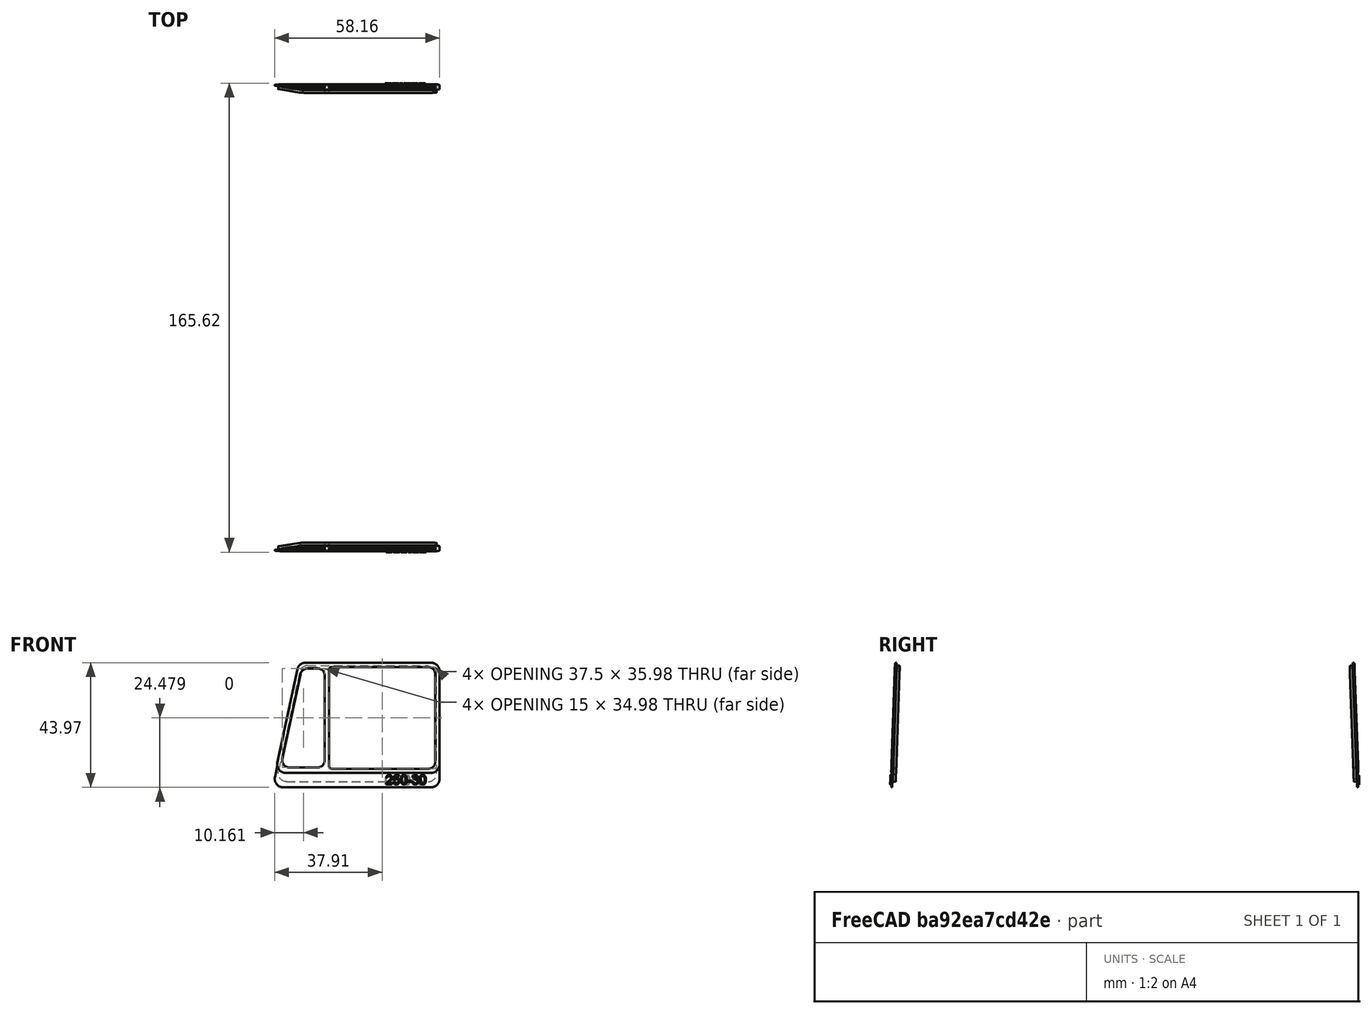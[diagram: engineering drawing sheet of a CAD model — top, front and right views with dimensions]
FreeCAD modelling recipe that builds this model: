
FCSTD DOCUMENT  (FreeCAD 0.16R4740 (Git))
Label: windows-fornt
License: All rights reserved
LicenseURL: http://en.wikipedia.org/wiki/All_rights_reserved
objects: Part::Box×24, Part::Fillet×22, Part::Cut×14, Part::MultiFuse×6, Part::Part2DObjectPython×2, Part::Extrusion×2, Part::Mirroring×2
note: 72 computed .brp shape members not serialized (recipe doc carries the construction recipe); baked Part::Feature solids carry a one-line shape summary decoded from their .brp

FEATURE [Part::Part2DObjectPython] ShapeString  # Draft 2D object (typed FeaturePython)
  FontFile = <path>
  Placement = pos=(57,0,71) rot=(1,0,0;1.5708rad)
  Size = 3.5
  String = 250-30
  Tracking = 0
FEATURE [Part::Extrusion] Extrude  label="front-left-window-frame-logo"
  Base = -> ShapeString
  Dir = (0,0.5,0)
  Placement = pos=(2,-0.4,-1.5) rot=(-1,0,0;0.036652rad)
  Solid = false
FEATURE [Part::Box] Box  label="Cube648"
  Height = 41
  Length = 57.5
  Placement = pos=(19.5,1,70.5) rot=(0,0,1;0rad)
  Width = 1
FEATURE [Part::Box] Box001  label="Cube649"
  Height = 48
  Length = 11
  Placement = pos=(9,0,70) rot=(0,1,0;0.20944rad)
  Width = 5
FEATURE [Part::Cut] Cut  label="Cut587"
  Base = -> Box
  Placement = pos=(0,-0.5,0) rot=(0,0,1;0rad)
  Tool = -> Box001
FEATURE [Part::Box] Box002  label="Cube650"
  Height = 39
  Length = 59
  Placement = pos=(19,0,73.5) rot=(0,0,1;0rad)
  Width = 0.5
FEATURE [Part::Box] Box003  label="Cube651"
  Height = 48
  Length = 11
  Placement = pos=(8,0,70) rot=(0,1,0;0.20944rad)
  Width = 5
FEATURE [Part::Cut] Cut001  label="Cut588"
  Base = -> Box002
  Tool = -> Box003
FEATURE [Part::Box] Box004  label="Cube652"
  Height = 35
  Length = 17
  Placement = pos=(20.5,0,75.5) rot=(0,0,1;0rad)
  Width = 5
FEATURE [Part::Box] Box005  label="Cube653"
  Height = 48
  Length = 11
  Placement = pos=(9.5,0,70) rot=(0,1,0;0.20944rad)
  Width = 5
FEATURE [Part::Cut] Cut002  label="Cut589"
  Base = -> Box004
  Tool = -> Box005
FEATURE [Part::Box] Box006  label="Cube654"
  Height = 36
  Length = 37.5
  Placement = pos=(39,0,75) rot=(0,0,1;0rad)
  Width = 5
FEATURE [Part::Fillet] Fillet
  Base = -> Box006
  Edges = 2 edges r=2.5: [Edge6,Edge8]
FEATURE [Part::Fillet] Fillet001
  Base = -> Fillet
  Edges = 2 edges r=1: [Edge17,Edge18]
FEATURE [Part::Fillet] Fillet002
  Base = -> Cut001
  Edges = 4 edges r=3: [Edge6,Edge7,Edge8,Edge11]
FEATURE [Part::Fillet] Fillet003
  Base = -> Cut
  Edges = 4 edges r=3: [Edge6,Edge7,Edge8,Edge11]
  Placement = pos=(0,0.2,0) rot=(0,0,1;0rad)
FEATURE [Part::Fillet] Fillet004
  Base = -> Fillet002
  Edges = 2 edges r=0.49: [Edge4,Edge5]
FEATURE [Part::Fillet] Fillet005
  Base = -> Cut002
  Edges = 4 edges r=2.5: [Edge6,Edge7,Edge8,Edge11]
FEATURE [Part::MultiFuse] Fusion001
  Shapes = -> [Fillet001,Fillet005]
FEATURE [Part::Box] Box007  label="Cube655"
  Height = 44
  Length = 59
  Placement = pos=(19,0.25,68.5) rot=(0,0,1;0rad)
  Width = 0.3
FEATURE [Part::Box] Box008  label="Cube656"
  Height = 48
  Length = 11
  Placement = pos=(8,0,69) rot=(0,1,0;0.20944rad)
  Width = 5
FEATURE [Part::Cut] Cut004  label="Cut591"
  Base = -> Box007
  Tool = -> Box008
FEATURE [Part::Fillet] Fillet007
  Base = -> Cut004
  Edges = 4 edges r=3: [Edge6,Edge7,Edge8,Edge11]
FEATURE [Part::Fillet] Fillet006
  Base = -> Fillet007
  Edges = 2 edges r=0.24: [Edge4,Edge5]
FEATURE [Part::Box] Box009  label="Cube657"
  Height = 35
  Length = 17
  Placement = pos=(20.5,0,75.5) rot=(0,0,1;0rad)
  Width = 5
FEATURE [Part::Box] Box010  label="Cube658"
  Height = 36
  Length = 37.5
  Placement = pos=(39,0,75) rot=(0,0,1;0rad)
  Width = 5
FEATURE [Part::Fillet] Fillet010
  Base = -> Box010
  Edges = 2 edges r=2.5: [Edge6,Edge8]
FEATURE [Part::Fillet] Fillet009
  Base = -> Fillet010
  Edges = 2 edges r=1: [Edge17,Edge18]
FEATURE [Part::Box] Box011  label="Cube659"
  Height = 48
  Length = 11
  Placement = pos=(9.5,0,70) rot=(0,1,0;0.20944rad)
  Width = 5
FEATURE [Part::Cut] Cut005  label="Cut592"
  Base = -> Box009
  Tool = -> Box011
FEATURE [Part::Fillet] Fillet008
  Base = -> Cut005
  Edges = 4 edges r=2.5: [Edge6,Edge7,Edge8,Edge11]
FEATURE [Part::MultiFuse] Fusion
  Shapes = -> [Fillet009,Fillet008]
FEATURE [Part::Cut] Cut006
  Base = -> Fillet003
  Placement = pos=(0,0,0) rot=(-1,0,0;0.034907rad)
  Tool = -> Fusion
FEATURE [Part::MultiFuse] Fusion002
  Shapes = -> [Fillet004,Fillet006]
FEATURE [Part::Cut] Cut007
  Base = -> Fusion002
  Placement = pos=(0,0,0) rot=(-1,0,0;0.034907rad)
  Tool = -> Fusion001
FEATURE [Part::Box] Box012  label="Cube660"
  Height = 41
  Length = 57.5
  Placement = pos=(19.5,1,70.5) rot=(0,0,1;0rad)
  Width = 1
FEATURE [Part::Box] Box013  label="Cube661"
  Height = 48
  Length = 11
  Placement = pos=(9,0,70) rot=(0,1,0;0.20944rad)
  Width = 5
FEATURE [Part::Cut] Cut008  label="Cut593"
  Base = -> Box012
  Placement = pos=(0,-0.5,0) rot=(0,0,1;0rad)
  Tool = -> Box013
FEATURE [Part::Fillet] Fillet011
  Base = -> Cut008
  Edges = 4 edges r=3: [Edge6,Edge7,Edge8,Edge11]
  Placement = pos=(0,0.2,0) rot=(0,0,1;0rad)
FEATURE [Part::Box] Box014  label="Cube662"
  Height = 35
  Length = 17
  Placement = pos=(20.5,0,75.5) rot=(0,0,1;0rad)
  Width = 5
FEATURE [Part::Box] Box015  label="Cube663"
  Height = 36
  Length = 37.5
  Placement = pos=(39,0,75) rot=(0,0,1;0rad)
  Width = 5
FEATURE [Part::Fillet] Fillet014
  Base = -> Box015
  Edges = 2 edges r=2.5: [Edge6,Edge8]
FEATURE [Part::Fillet] Fillet013
  Base = -> Fillet014
  Edges = 2 edges r=1: [Edge17,Edge18]
FEATURE [Part::Box] Box016  label="Cube664"
  Height = 48
  Length = 11
  Placement = pos=(9.5,0,70) rot=(0,1,0;0.20944rad)
  Width = 5
FEATURE [Part::Cut] Cut009  label="Cut594"
  Base = -> Box014
  Tool = -> Box016
FEATURE [Part::Fillet] Fillet012
  Base = -> Cut009
  Edges = 4 edges r=2.5: [Edge6,Edge7,Edge8,Edge11]
FEATURE [Part::MultiFuse] Fusion003
  Shapes = -> [Fillet013,Fillet012]
FEATURE [Part::Cut] Cut010
  Base = -> Fillet011
  Placement = pos=(0,0,0) rot=(-1,0,0;0.034907rad)
  Tool = -> Fusion003
FEATURE [Part::Mirroring] Part__Mirroring  label="Cut010 (Mirror #1)"
  Base = (0,0,0)
  Normal = (0,1,0)
  Placement = pos=(0,170,0) rot=(0,0,1;0rad)
  Source = -> Cut010
FEATURE [Part::Box] Box017  label="Cube665"
  Height = 39
  Length = 59
  Placement = pos=(19,0,73.5) rot=(0,0,1;0rad)
  Width = 0.5
FEATURE [Part::Box] Box018  label="Cube666"
  Height = 48
  Length = 11
  Placement = pos=(8,0,70) rot=(0,1,0;0.20944rad)
  Width = 5
FEATURE [Part::Cut] Cut011  label="Cut595"
  Base = -> Box017
  Tool = -> Box018
FEATURE [Part::Box] Box019  label="Cube667"
  Height = 35
  Length = 17
  Placement = pos=(20.5,0,75.5) rot=(0,0,1;0rad)
  Width = 5
FEATURE [Part::Box] Box020  label="Cube668"
  Height = 48
  Length = 11
  Placement = pos=(9.5,0,70) rot=(0,1,0;0.20944rad)
  Width = 5
FEATURE [Part::Cut] Cut012  label="Cut596"
  Base = -> Box019
  Tool = -> Box020
FEATURE [Part::Box] Box021  label="Cube669"
  Height = 36
  Length = 37.5
  Placement = pos=(39,0,75) rot=(0,0,1;0rad)
  Width = 5
FEATURE [Part::Fillet] Fillet015
  Base = -> Box021
  Edges = 2 edges r=2.5: [Edge6,Edge8]
FEATURE [Part::Fillet] Fillet016
  Base = -> Fillet015
  Edges = 2 edges r=1: [Edge17,Edge18]
FEATURE [Part::Fillet] Fillet017
  Base = -> Cut011
  Edges = 4 edges r=3: [Edge6,Edge7,Edge8,Edge11]
FEATURE [Part::Fillet] Fillet018
  Base = -> Fillet017
  Edges = 2 edges r=0.49: [Edge4,Edge5]
FEATURE [Part::Fillet] Fillet019
  Base = -> Cut012
  Edges = 4 edges r=2.5: [Edge6,Edge7,Edge8,Edge11]
FEATURE [Part::MultiFuse] Fusion004
  Shapes = -> [Fillet016,Fillet019]
FEATURE [Part::Box] Box022  label="Cube670"
  Height = 44
  Length = 59
  Placement = pos=(19,0.25,68.5) rot=(0,0,1;0rad)
  Width = 0.3
FEATURE [Part::Box] Box023  label="Cube671"
  Height = 48
  Length = 11
  Placement = pos=(8,0,69) rot=(0,1,0;0.20944rad)
  Width = 5
FEATURE [Part::Cut] Cut013  label="Cut597"
  Base = -> Box022
  Tool = -> Box023
FEATURE [Part::Fillet] Fillet021
  Base = -> Cut013
  Edges = 4 edges r=3: [Edge6,Edge7,Edge8,Edge11]
FEATURE [Part::Fillet] Fillet020
  Base = -> Fillet021
  Edges = 2 edges r=0.24: [Edge4,Edge5]
FEATURE [Part::MultiFuse] Fusion005
  Shapes = -> [Fillet018,Fillet020]
FEATURE [Part::Cut] Cut014
  Base = -> Fusion005
  Placement = pos=(0,0,0) rot=(-1,0,0;0.034907rad)
  Tool = -> Fusion004
FEATURE [Part::Mirroring] Part__Mirroring001  label="Cut014 (Mirror #2)"
  Base = (0,0,0)
  Normal = (0,1,0)
  Placement = pos=(0,170,0) rot=(0,0,1;0rad)
  Source = -> Cut014
FEATURE [Part::Part2DObjectPython] ShapeString001  # Draft 2D object (typed FeaturePython)
  FontFile = <path>
  Placement = pos=(57,0,71) rot=(1,0,0;1.5708rad)
  Size = 3.5
  String = 250-30
  Tracking = 0
FEATURE [Part::Extrusion] Extrude001  label="front-right-window-frame-logo"
  Base = -> ShapeString001
  Dir = (0,0.5,0)
  Placement = pos=(130,170.424,-1.6) rot=(0,-0.018325,0.999832;3.14159rad)
  Solid = false
note: 2 file-system paths scrubbed to <path> (originals preserved in the JSON sidecar)
